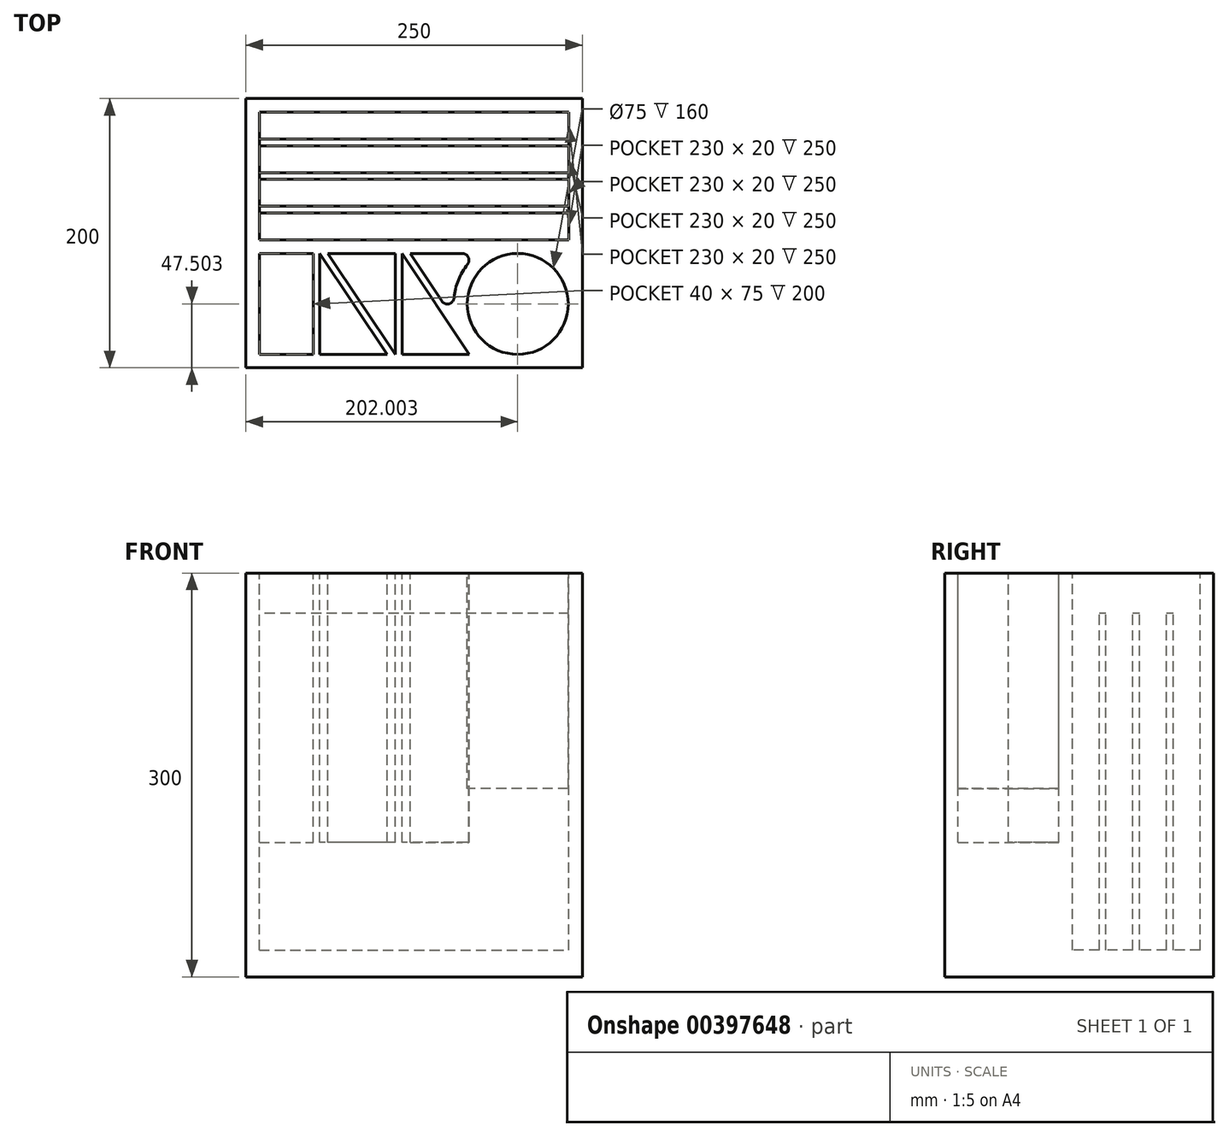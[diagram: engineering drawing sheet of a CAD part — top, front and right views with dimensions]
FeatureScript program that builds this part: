
annotation { "Feature Type Name" : "Feature", "Feature Type Description" : "" }
export const myFeature = defineFeature(function(context is Context, id is Id, definition is map)
    precondition{}
    {
        {
            var Q0;
            Q0=qCreatedBy(makeId("Top.planeOp"),FACE);
            var sketch = newSketch(context, id + "F0", { "sketchPlane" : qUnion([Q0])});
            skLineSegment(sketch, "E0.bottom", {"start": v(-124.16, 105.34) * mm, "end": v(125.84, 105.34) * mm});
            skLineSegment(sketch, "E0.top", {"start": v(-124.16, -94.66) * mm, "end": v(125.84, -94.66) * mm});
            skLineSegment(sketch, "E0.left", {"start": v(-124.16, 105.34) * mm, "end": v(-124.16, -94.66) * mm});
            skLineSegment(sketch, "E0.right", {"start": v(125.84, 105.34) * mm, "end": v(125.84, -94.66) * mm});
            skSolve(sketch);
        }
        {
            var Q0;
            Q0 = qSketchRegion(id + "F0", true);
            extrude(context, id + "F1", {"entities" : qUnion([Q0]), "depth" : 300 * mm});
        }
        {
            var Q0;
            Q0=makeQuery(id+"F1.opExtrude","CAP_FACE",FACE,{"disambiguationData":[OSD([sQuery(id+"F0.wireOp",EDGE,"E0.bottom"),sQuery(id+"F0.wireOp",EDGE,"E0.top"),sQuery(id+"F0.wireOp",EDGE,"E0.left"),sQuery(id+"F0.wireOp",EDGE,"E0.right")])],"isStart":false});
            var sketch = newSketch(context, id + "F2", { "sketchPlane" : qUnion([Q0])});
            skLineSegment(sketch, "E1.bottom", {"start": v(-114.16, 95.34) * mm, "end": v(115.84, 95.34) * mm});
            skLineSegment(sketch, "E1.top", {"start": v(-114.16, 75.34) * mm, "end": v(115.84, 75.34) * mm});
            skLineSegment(sketch, "E1.left", {"start": v(-114.16, 95.34) * mm, "end": v(-114.16, 75.34) * mm});
            skLineSegment(sketch, "E1.right", {"start": v(115.84, 95.34) * mm, "end": v(115.84, 75.34) * mm});
            skLineSegment(sketch, "E2.bottom", {"start": v(-114.16, 70.34) * mm, "end": v(115.84, 70.34) * mm});
            skLineSegment(sketch, "E2.top", {"start": v(-114.16, 50.34) * mm, "end": v(115.84, 50.34) * mm});
            skLineSegment(sketch, "E2.left", {"start": v(-114.16, 70.34) * mm, "end": v(-114.16, 50.34) * mm});
            skLineSegment(sketch, "E2.right", {"start": v(115.84, 70.34) * mm, "end": v(115.84, 50.34) * mm});
            skLineSegment(sketch, "E3.bottom", {"start": v(-114.16, 45.34) * mm, "end": v(115.84, 45.34) * mm});
            skLineSegment(sketch, "E3.top", {"start": v(-114.16, 25.34) * mm, "end": v(115.84, 25.34) * mm});
            skLineSegment(sketch, "E3.left", {"start": v(-114.16, 45.34) * mm, "end": v(-114.16, 25.34) * mm});
            skLineSegment(sketch, "E3.right", {"start": v(115.84, 45.34) * mm, "end": v(115.84, 25.34) * mm});
            skLineSegment(sketch, "E4.bottom", {"start": v(-114.16, 20.34) * mm, "end": v(115.84, 20.34) * mm});
            skLineSegment(sketch, "E4.top", {"start": v(-114.16, 0.34) * mm, "end": v(115.84, 0.34) * mm});
            skLineSegment(sketch, "E4.left", {"start": v(-114.16, 20.34) * mm, "end": v(-114.16, 0.34) * mm});
            skLineSegment(sketch, "E4.right", {"start": v(115.84, 20.34) * mm, "end": v(115.84, 0.34) * mm});
            skSolve(sketch);
        }
        {
            var Q0;
            Q0 = qSketchRegion(id + "F2", true);
            extrude(context, id + "F3", {"entities" : qUnion([Q0]), "operationType" : NewBodyOperationType.REMOVE, "oppositeDirection" : true, "depth" : 280 * mm});
        }
        {
            var Q0;
            Q0=makeQuery(id+"F1.opExtrude","CAP_FACE",FACE,{"disambiguationData":[OSD([sQuery(id+"F0.wireOp",EDGE,"E0.bottom"),sQuery(id+"F0.wireOp",EDGE,"E0.top"),sQuery(id+"F0.wireOp",EDGE,"E0.left"),sQuery(id+"F0.wireOp",EDGE,"E0.right")])],"isStart":false});
            var sketch = newSketch(context, id + "F4", { "sketchPlane" : qUnion([Q0])});
            skLineSegment(sketch, "E5.bottom", {"start": v(-114.16, 75.34) * mm, "end": v(115.84, 75.34) * mm});
            skLineSegment(sketch, "E5.top", {"start": v(-114.16, 20.34) * mm, "end": v(115.84, 20.34) * mm});
            skLineSegment(sketch, "E5.left", {"start": v(-114.16, 75.34) * mm, "end": v(-114.16, 20.34) * mm});
            skLineSegment(sketch, "E5.right", {"start": v(115.84, 75.34) * mm, "end": v(115.84, 20.34) * mm});
            skSolve(sketch);
        }
        {
            var Q0;
            Q0 = qSketchRegion(id + "F4", true);
            extrude(context, id + "F5", {"entities" : qUnion([Q0]), "operationType" : NewBodyOperationType.REMOVE, "oppositeDirection" : true, "depth" : 30 * mm});
        }
        {
            var Q0;
            Q0=makeQuery(id+"F1.opExtrude","CAP_FACE",FACE,{"disambiguationData":[OSD([sQuery(id+"F0.wireOp",EDGE,"E0.bottom"),sQuery(id+"F0.wireOp",EDGE,"E0.top"),sQuery(id+"F0.wireOp",EDGE,"E0.left"),sQuery(id+"F0.wireOp",EDGE,"E0.right")])],"isStart":false});
            var sketch = newSketch(context, id + "F6", { "sketchPlane" : qUnion([Q0])});
            skLineSegment(sketch, "E6.bottom", {"start": v(36.61, -9.66) * mm, "end": v(-114.16, -9.66) * mm, "construction": true});
            skLineSegment(sketch, "E6.top", {"start": v(115.84, -84.66) * mm, "end": v(-114.16, -84.66) * mm, "construction": true});
            skLineSegment(sketch, "E6.left", {"start": v(115.84, -9.66) * mm, "end": v(115.84, -84.66) * mm, "construction": true});
            skLineSegment(sketch, "E6.right", {"start": v(-114.16, -9.66) * mm, "end": v(-114.16, -84.66) * mm, "construction": true});
            skCircle(sketch, "E7", {"center": v(77.84, -47.16) * mm, "radius": 37.5 * mm});
            skPoint(sketch, "E7.centerSnap0", {"position": v(115.84, -47.16) * mm});
            skLineSegment(sketch, "E8.bottom", {"start": v(-114.16, -84.66) * mm, "end": v(-74.16, -84.66) * mm});
            skLineSegment(sketch, "E8.top", {"start": v(-114.16, -9.66) * mm, "end": v(-74.16, -9.66) * mm});
            skLineSegment(sketch, "E8.left", {"start": v(-114.16, -84.66) * mm, "end": v(-114.16, -9.66) * mm});
            skLineSegment(sketch, "E8.right", {"start": v(-74.16, -84.66) * mm, "end": v(-74.16, -9.66) * mm});
            skLineSegment(sketch, "E9", {"start": v(-69.16, -9.66) * mm, "end": v(-69.16, -84.66) * mm});
            skLineSegment(sketch, "E10", {"start": v(-69.16, -84.66) * mm, "end": v(-19.16, -84.66) * mm});
            skLineSegment(sketch, "E11", {"start": v(-19.16, -84.66) * mm, "end": v(-69.16, -9.66) * mm});
            skLineSegment(sketch, "E12", {"start": v(-63.15, -9.66) * mm, "end": v(-13.15, -84.66) * mm});
            skLineSegment(sketch, "E13", {"start": v(-13.15, -84.66) * mm, "end": v(-13.15, -9.66) * mm});
            skLineSegment(sketch, "E14", {"start": v(-13.15, -9.66) * mm, "end": v(-63.15, -9.66) * mm});
            skLineSegment(sketch, "E15", {"start": v(-8.15, -84.66) * mm, "end": v(-8.15, -9.66) * mm});
            skLineSegment(sketch, "E16", {"start": v(-8.15, -9.66) * mm, "end": v(41.85, -84.66) * mm});
            skLineSegment(sketch, "E17", {"start": v(41.85, -84.66) * mm, "end": v(-8.15, -84.66) * mm});
            skLineSegment(sketch, "E18", {"start": v(-2.14, -9.66) * mm, "end": v(21.42, -44.99) * mm});
            skArc(sketch, "E19", {"start": v(30.55, -42.69) * mm, "mid": v(33.75, -29.5) * mm, "end": v(40.54, -17.75) * mm});
            skLineSegment(sketch, "E20", {"start": v(-2.14, -9.66) * mm, "end": v(49.19, -9.66) * mm});
            skPoint(sketch, "E21.newPointB", {"position": v(115.84, -9.66) * mm});
            skArc(sketch, "E21.filletArc", {"start": v(40.54, -17.75) * mm, "mid": v(41.11, -12.48) * mm, "end": v(36.61, -9.66) * mm});
            skArc(sketch, "E22.filletArc", {"start": v(21.42, -44.99) * mm, "mid": v(26.8, -47.06) * mm, "end": v(30.55, -42.69) * mm});
            skSolve(sketch);
        }
        {
            var Q0;
            Q0=makeQuery(id+"F6.imprint","IMPRINT",FACE,{"disambiguationData":[TD([[makeQuery(id+"F6.imprint","IMPRINT",EDGE,{"derivedFrom":sQuery(id+"F6.wireOp",EDGE,"E7")}),1.0]])]});
            extrude(context, id + "F7", {"entities" : qUnion([Q0]), "operationType" : NewBodyOperationType.REMOVE, "oppositeDirection" : true, "depth" : 160 * mm});
        }
        {
            var Q0;
            Q0=makeQuery(id+"F6.imprint","IMPRINT",FACE,{"disambiguationData":[TD([[makeQuery(id+"F6.imprint","IMPRINT",EDGE,{"derivedFrom":sQuery(id+"F6.wireOp",EDGE,"E8.bottom")}),1.0]])]});
            var Q1;
            Q1=makeQuery(id+"F6.imprint","IMPRINT",FACE,{"disambiguationData":[TD([[makeQuery(id+"F6.imprint","IMPRINT",EDGE,{"derivedFrom":sQuery(id+"F6.wireOp",EDGE,"E9")}),1.0]])]});
            var Q2;
            Q2=makeQuery(id+"F6.imprint","IMPRINT",FACE,{"disambiguationData":[TD([[makeQuery(id+"F6.imprint","IMPRINT",EDGE,{"derivedFrom":sQuery(id+"F6.wireOp",EDGE,"E12")}),1.0]])]});
            var Q3;
            Q3=makeQuery(id+"F6.imprint","IMPRINT",FACE,{"disambiguationData":[TD([[makeQuery(id+"F6.imprint","IMPRINT",EDGE,{"derivedFrom":sQuery(id+"F6.wireOp",EDGE,"E15")}),-1.0]])]});
            var Q4;
            {var subQ2=sQuery(id+"F6.wireOp",EDGE,"E18");Q4=makeQuery(id+"F6.imprint","IMPRINT",FACE,{"disambiguationData":[TD([[makeQuery(id+"F6.imprint","IMPRINT",EDGE,{"derivedFrom":subQ2}),1.0]])]});}
            extrude(context, id + "F8", {"entities" : qUnion([Q0, Q1, Q2, Q3, Q4]), "operationType" : NewBodyOperationType.REMOVE, "oppositeDirection" : true, "depth" : 200 * mm});
        }
    });
